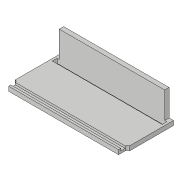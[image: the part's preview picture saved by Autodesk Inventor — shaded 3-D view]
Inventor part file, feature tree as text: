
AUTODESK INVENTOR PART (.ipt)
format: ipt  version: 2018.3 (Build 223284000, 284)  size: 137,216 bytes
history: native  units: in
note: dims shown in document units (in); Inventor stores cm internally (conversion verified against a paired STEP export)
features: extrude x5, sketch x5, fillet x1
ambient origin geometry x8: Origin, YZ Plane, XZ Plane, XY Plane, X Axis, Y Axis, Z Axis, Center Point
bodies: Solid1 (feature_tree)
feature tree (11):
  extrude  "Extrusion1"  Depth=1.5in
  extrude  "Extrusion2"  Depth=0.126in
  extrude  "Extrusion3"  Depth=0.0625in
  extrude  "Extrusion4"  Depth=0.135in
  fillet  "Fillet1"  Radius=0.125in
  extrude  "Extrusion5"  Depth=0.135in
  sketch  "Sketch1"  dims[d0=3.25in d1=1.5in]
  sketch  "Sketch2"  dims[d2=0.125in d3=0.0in d4=0.126in]
  sketch  "Sketch3"  dims[d5=0.0625in d8=3.375in]
  sketch  "Sketch4"  dims[d9=0.0625in d10=0.135in d11=0.125in]
  sketch  "Sketch5"  dims[d12=0.0625in d13=0.0in d15=0.135in d16=0.125in d17=0.0625in d18=0.5in d19=0.0in d20=0.0625in d21=0.0625in d22=0.25in d23=0.25in d24=0.0625in d25=0.5in d26=0.0in d27=0.0625in d29=0.75in d30=0.0in d31=0.125in d32=0.126in d33=0.126in]
